# Revit family: HVAC_Ductwork_Airzone_Swirl-Diffuser_DRPL-PX1
name_source: partatom
category: Air Terminals
revit_build: Autodesk Revit 2016 (Build: 20161004_0715(x64)
units: mm (PartAtom-declared; Revit-internal decimal feet)

## family parameters
Cut with Voids When Loaded = No
Host = Face
OmniClass Number = 23.75.70.21
OmniClass Title = Terminals for Air
Part Type = Normal
Room Calculation Point = Yes
Round Connector Dimension = Use Diameter
Shared = No

## types (1)
- INVALID TYPE - Use Load Family and Type Catalog
    Accessories Material = Metal - AIRZONE - Galvanized Sheet - Semi-polished
    Ak = 2
    Compatible Accesories = Insulated flexible duct (TFTA) and non-insulated flexible duct (TFST)
Insulated plenum for round duct diffusers (PLEADROT) and non-insulated plenum for round duct diffusers (PLEDROT)
    Default Elevation = 0 mm
    Description = Swirl diffuser for modular ceiling
    Disclaimer = All information provided in this model is reviewed before being published. However, Airzone cannot guarantee this model is error-free, therefore users are strongly encouraged to check for technical documentation and updates
    Duct Diameter = 200 mm
    Effective Area = 200.00 cm²
    Element Material = Hollow - AIRZONE - Deep Black
    Finish = White (RAL 9010)
    Fixing = Modular ceiling profile
    Front Type = DRPL_Diffuser : 12 Elements
    Long Description = Square swirl diffuser DRPL integrated in plaque to enable the air flow supply creating an efficient swirl. Designed to be installed in HVAC ducted networks.
    Main Material = Metal - AIRZONE - Steel Sheet - White (RAL 9010)
    Manufacturer = AIRZONE
    Max Flow = 600 m³/h
    Min Flow = 100 m³/h
    Model = INVALID – Type not loaded via type catalog
    Product Code = INVALID – Type not loaded via type catalog
    Product Comments = Refer to technical documentation for further details
    Product Documentation Download URL = http://doc.airzone.es
    Revit Model Version = 1.0
    Type Image Comments = Image available in product documentation download
    URL = www.airzone.es
    c1 = 0.000479
    c2 = -1.683
    c3 = -23.62
    c4 = -253.5
    c5 = 32.08
    c6 = 73.32
    c7 = 0.02258
    c8 = -0.9302

## geometry (parser evidence)
native form markers: Sweep x11
no freeform markers — native parametric forms only
